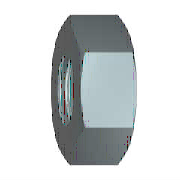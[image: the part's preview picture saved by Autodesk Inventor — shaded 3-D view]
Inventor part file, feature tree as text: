
AUTODESK INVENTOR PART (.ipt)
format: ipt  version: 2015 (Build 190159000, 159)  size: 177,664 bytes
history: native  units: mm (DEFAULTED — no unit token found)
features: sketch x3, other x2, extrude x1, hole x1, plane x1
ambient origin geometry x7: Origin, YZ Plane, XZ Plane, X Axis, Y Axis, Z Axis, Center Point
bodies: Body1 (feature_tree)
feature tree (8):
  extrude  "Bryła"  Depth=20.78461mm
  other  "Faza1"
  hole  "Gwint"  [1 undecoded]
  other  "Work Axis1"
  plane  "Work Plane1"
  sketch  "Szkic1"
  sketch  "Szkic2"
  sketch  "Szkic3"
note: 1 required parameter value undecoded (feature->parameter linkage not recoverable at this tier; creation-order binding heuristic only, values carry confidence <= 0.55)
